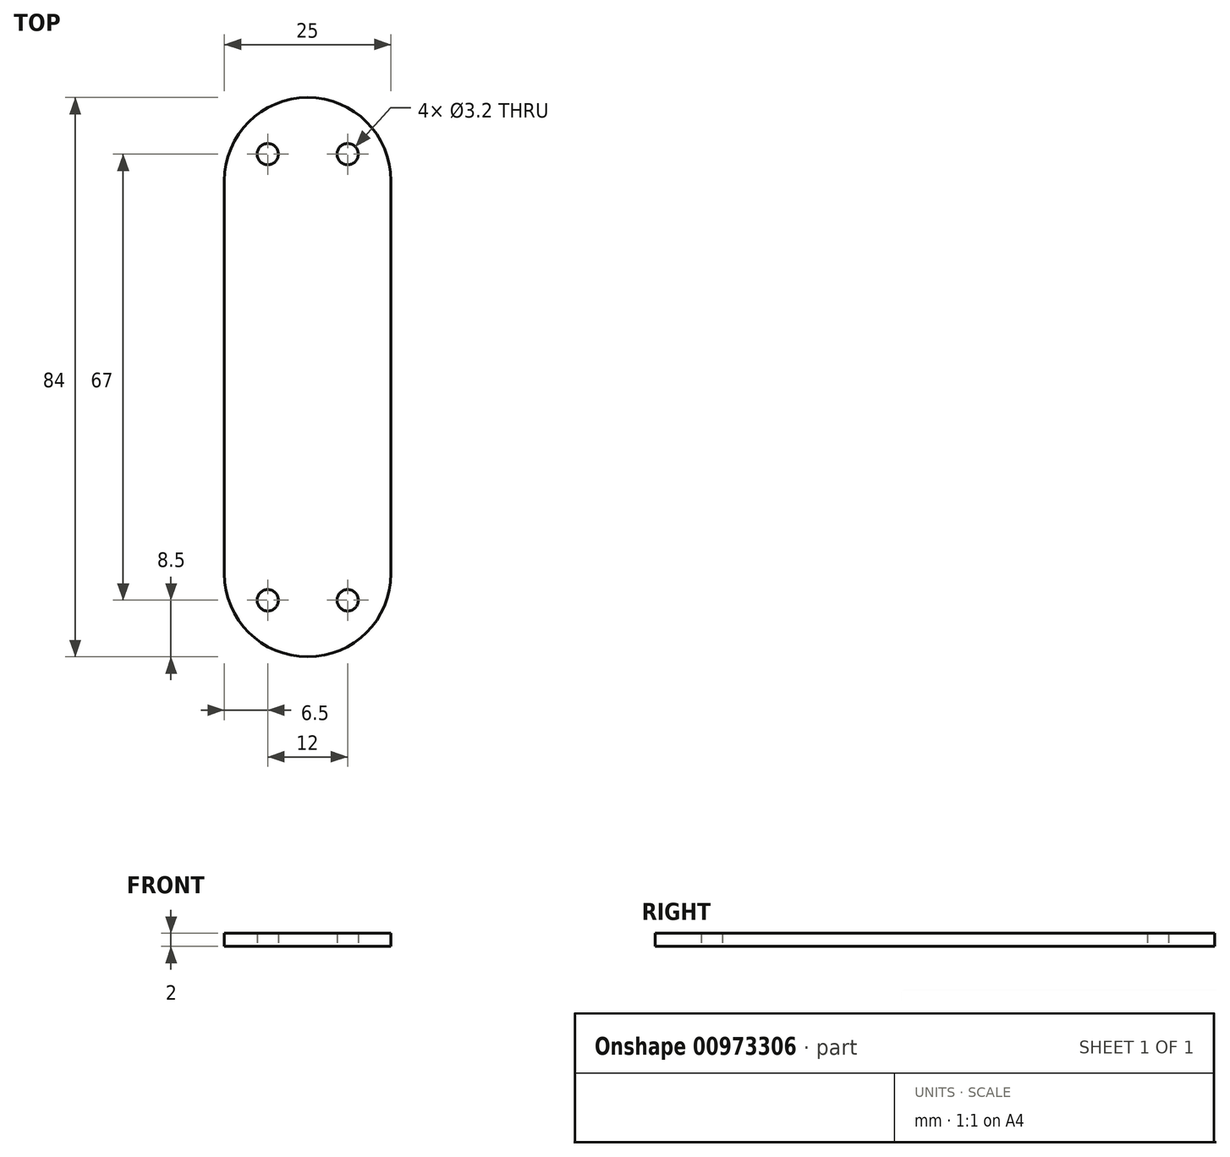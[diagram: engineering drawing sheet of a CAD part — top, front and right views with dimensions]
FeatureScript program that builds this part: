
annotation { "Feature Type Name" : "Feature", "Feature Type Description" : "" }
export const myFeature = defineFeature(function(context is Context, id is Id, definition is map)
    precondition{}
    {
        {
            var Q0;
            Q0=qCreatedBy(makeId("Top.planeOp"),FACE);
            var sketch = newSketch(context, id + "F0", { "sketchPlane" : qUnion([Q0])});
            skLineSegment(sketch, "E0.bottom", {"start": v(10.5, 27.5) * mm, "end": v(-10.5, 27.5) * mm, "construction": true});
            skLineSegment(sketch, "E0.top", {"start": v(10.5, -27.5) * mm, "end": v(-10.5, -27.5) * mm, "construction": true});
            skLineSegment(sketch, "E0.left", {"start": v(10.5, 27.5) * mm, "end": v(10.5, -27.5) * mm, "construction": true});
            skLineSegment(sketch, "E0.right", {"start": v(-10.5, 27.5) * mm, "end": v(-10.5, -27.5) * mm, "construction": true});
            skPoint(sketch, "E0.middle", {"position": v(0, 0) * mm});
            skLineSegment(sketch, "E1.left", {"start": v(12.5, 29.5) * mm, "end": v(12.5, -29.5) * mm});
            skLineSegment(sketch, "E1.right", {"start": v(-12.5, 29.5) * mm, "end": v(-12.5, -29.5) * mm});
            skArc(sketch, "E2", {"start": v(12.5, 29.5) * mm, "mid": v(0, 42) * mm, "end": v(-12.5, 29.5) * mm});
            skArc(sketch, "E3.MirrorCS", {"start": v(12.5, -29.5) * mm, "mid": v(0, -42) * mm, "end": v(-12.5, -29.5) * mm});
            skCircle(sketch, "E4", {"center": v(-6, 33.5) * mm, "radius": 1.6 * mm});
            skCircle(sketch, "E5.MirrorC", {"center": v(6, 33.5) * mm, "radius": 1.6 * mm});
            skCircle(sketch, "E6.MirrorC", {"center": v(-6, -33.5) * mm, "radius": 1.6 * mm});
            skCircle(sketch, "E7.MirrorC", {"center": v(6, -33.5) * mm, "radius": 1.6 * mm});
            skSolve(sketch);
        }
        {
            var Q0;
            Q0=makeQuery(id+"F0.imprint","IMPRINT",FACE,{"disambiguationData":[TD([[makeQuery(id+"F0.imprint","IMPRINT",EDGE,{"derivedFrom":sQuery(id+"F0.wireOp",EDGE,"E0.bottom")}),-1.0]])]});
            var Q1;
            Q1=makeQuery(id+"F0.imprint","IMPRINT",FACE,{"disambiguationData":[TD([[makeQuery(id+"F0.imprint","IMPRINT",EDGE,{"derivedFrom":sQuery(id+"F0.wireOp",EDGE,"E1.left")}),-1.0]])]});
            extrude(context, id + "F1", {"entities" : qUnion([Q0, Q1]), "depth" : 2 * mm, "offsetDistance" : 25 * mm});
        }
    });
